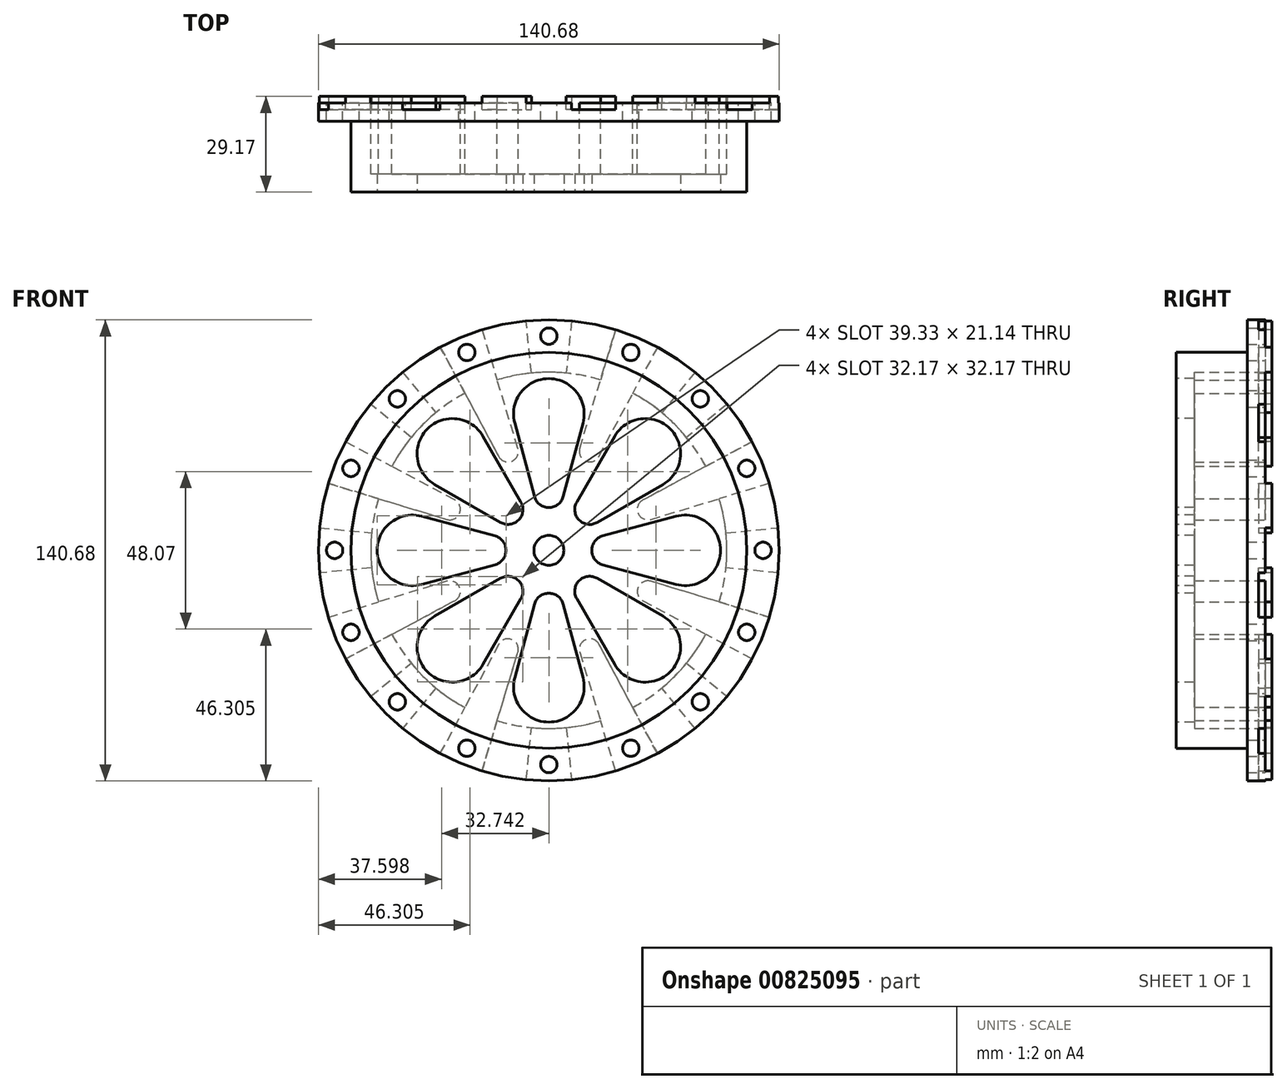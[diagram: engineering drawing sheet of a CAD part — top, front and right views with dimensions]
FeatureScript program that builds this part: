
annotation { "Feature Type Name" : "Feature", "Feature Type Description" : "" }
export const myFeature = defineFeature(function(context is Context, id is Id, definition is map)
    precondition{}
    {
        {
            var Q0;
            Q0=qCreatedBy(makeId("Right.planeOp"),FACE);
            var sketch = newSketch(context, id + "F0", { "sketchPlane" : qUnion([Q0])});
            skLineSegment(sketch, "E0", {"start": v(-27.17, 0) * mm, "end": v(-27.17, 60.4) * mm});
            skLineSegment(sketch, "E1", {"start": v(-21.65, 54.34) * mm, "end": v(-21.65, 0) * mm});
            skLineSegment(sketch, "E2", {"start": v(-21.65, 0) * mm, "end": v(-27.17, 0) * mm});
            skLineSegment(sketch, "E3", {"start": v(-27.17, 60.4) * mm, "end": v(-5.52, 60.4) * mm});
            skLineSegment(sketch, "E4", {"start": v(-21.65, 54.34) * mm, "end": v(0, 54.34) * mm});
            skLineSegment(sketch, "E5", {"start": v(-5.52, 60.4) * mm, "end": v(-5.52, 70.34) * mm});
            skLineSegment(sketch, "E6", {"start": v(-5.52, 70.34) * mm, "end": v(0, 70.34) * mm});
            skLineSegment(sketch, "E7", {"start": v(0, 70.34) * mm, "end": v(0, 54.34) * mm});
            skSolve(sketch);
        }
        {
            var Q0;
            Q0=makeQuery(id+"F0.imprint","IMPRINT",FACE,{"disambiguationData":[TD([[makeQuery(id+"F0.imprint","IMPRINT",EDGE,{"derivedFrom":sQuery(id+"F0.wireOp",EDGE,"E0")}),-1.0]])]});
            var Q1;
            Q1=sQuery(id+"F0.wireOp",EDGE,"E2");
            revolve(context, id + "F1", {"surfaceOperationType" : NewSurfaceOperationType.NEW, "entities" : qUnion([Q0]), "axis" : qUnion([Q1]), "revolveType" : RevolveType.FULL});
        }
        {
            var Q0;
            Q0=qCreatedBy(makeId("Front.planeOp"),FACE);
            var sketch = newSketch(context, id + "F2", { "sketchPlane" : qUnion([Q0])});
            skPoint(sketch, "E8", {"position": v(0, 65.37) * mm});
            skPoint(sketch, "E9.center", {"position": v(0, 0) * mm});
            skLineSegment(sketch, "E10.2.23.0", {"start": v(4.41, 16.46) * mm, "end": v(10.4, 38.84) * mm});
            skArc(sketch, "E11", {"start": v(-4.41, 16.46) * mm, "mid": v(0, 13.08) * mm, "end": v(4.41, 16.46) * mm});
            skArc(sketch, "E12", {"start": v(10.4, 38.84) * mm, "mid": v(0, 52.4) * mm, "end": v(-10.4, 38.84) * mm});
            skLineSegment(sketch, "E13", {"start": v(-10.4, 38.84) * mm, "end": v(-4.41, 16.46) * mm});
            skArc(sketch, "E14.1.0", {"start": v(-20.1, 34.83) * mm, "mid": v(-37.06, 37.06) * mm, "end": v(-34.83, 20.1) * mm});
            skLineSegment(sketch, "E14.1.1", {"start": v(-8.52, 14.76) * mm, "end": v(-20.1, 34.83) * mm});
            skArc(sketch, "E14.1.2", {"start": v(-14.76, 8.52) * mm, "mid": v(-9.25, 9.25) * mm, "end": v(-8.52, 14.76) * mm});
            skLineSegment(sketch, "E14.1.3", {"start": v(-34.83, 20.1) * mm, "end": v(-14.76, 8.52) * mm});
            skArc(sketch, "E14.2.0", {"start": v(-38.84, 10.4) * mm, "mid": v(-52.4, 0) * mm, "end": v(-38.84, -10.4) * mm});
            skLineSegment(sketch, "E14.2.1", {"start": v(-16.46, 4.41) * mm, "end": v(-38.84, 10.4) * mm});
            skArc(sketch, "E14.2.2", {"start": v(-16.46, -4.41) * mm, "mid": v(-13.08, 0) * mm, "end": v(-16.46, 4.41) * mm});
            skLineSegment(sketch, "E14.2.3", {"start": v(-38.84, -10.4) * mm, "end": v(-16.46, -4.41) * mm});
            skArc(sketch, "E14.3.0", {"start": v(-34.83, -20.1) * mm, "mid": v(-37.06, -37.06) * mm, "end": v(-20.1, -34.83) * mm});
            skLineSegment(sketch, "E14.3.1", {"start": v(-14.76, -8.52) * mm, "end": v(-34.83, -20.1) * mm});
            skArc(sketch, "E14.3.2", {"start": v(-8.52, -14.76) * mm, "mid": v(-9.25, -9.25) * mm, "end": v(-14.76, -8.52) * mm});
            skLineSegment(sketch, "E14.3.3", {"start": v(-20.1, -34.83) * mm, "end": v(-8.52, -14.76) * mm});
            skArc(sketch, "E14.4.0", {"start": v(-10.4, -38.84) * mm, "mid": v(0, -52.4) * mm, "end": v(10.4, -38.84) * mm});
            skLineSegment(sketch, "E14.4.1", {"start": v(-4.41, -16.46) * mm, "end": v(-10.4, -38.84) * mm});
            skArc(sketch, "E14.4.2", {"start": v(4.41, -16.46) * mm, "mid": v(0, -13.08) * mm, "end": v(-4.41, -16.46) * mm});
            skLineSegment(sketch, "E14.4.3", {"start": v(10.4, -38.84) * mm, "end": v(4.41, -16.46) * mm});
            skArc(sketch, "E14.5.0", {"start": v(20.1, -34.83) * mm, "mid": v(37.06, -37.06) * mm, "end": v(34.83, -20.1) * mm});
            skLineSegment(sketch, "E14.5.1", {"start": v(8.52, -14.76) * mm, "end": v(20.1, -34.83) * mm});
            skArc(sketch, "E14.5.2", {"start": v(14.76, -8.52) * mm, "mid": v(9.25, -9.25) * mm, "end": v(8.52, -14.76) * mm});
            skLineSegment(sketch, "E14.5.3", {"start": v(34.83, -20.1) * mm, "end": v(14.76, -8.52) * mm});
            skPoint(sketch, "E15.1.0", {"position": v(-25.02, 60.4) * mm});
            skPoint(sketch, "E15.2.0", {"position": v(-46.23, 46.23) * mm});
            skPoint(sketch, "E15.3.0", {"position": v(-60.4, 25.02) * mm});
            skPoint(sketch, "E15.4.0", {"position": v(-65.37, 0) * mm});
            skPoint(sketch, "E15.5.0", {"position": v(-60.4, -25.02) * mm});
            skPoint(sketch, "E16.0.6.0", {"position": v(-46.23, -46.23) * mm});
            skPoint(sketch, "E16.0.7.0", {"position": v(-25.02, -60.4) * mm});
            skPoint(sketch, "E16.0.8.0", {"position": v(0, -65.37) * mm});
            skPoint(sketch, "E16.0.9.0", {"position": v(25.02, -60.4) * mm});
            skPoint(sketch, "E16.0.10.0", {"position": v(46.23, -46.23) * mm});
            skPoint(sketch, "E16.0.11.0", {"position": v(60.4, -25.02) * mm});
            skCircle(sketch, "E17", {"center": v(0, 0) * mm, "radius": 4.57 * mm});
            skArc(sketch, "E18.3.6.0", {"start": v(38.84, -10.4) * mm, "mid": v(52.4, 0) * mm, "end": v(38.84, 10.4) * mm});
            skLineSegment(sketch, "E18.4.6.0", {"start": v(16.46, -4.41) * mm, "end": v(38.84, -10.4) * mm});
            skArc(sketch, "E18.7.6.0", {"start": v(16.46, 4.41) * mm, "mid": v(13.08, 0) * mm, "end": v(16.46, -4.41) * mm});
            skLineSegment(sketch, "E18.11.6.0", {"start": v(38.84, 10.4) * mm, "end": v(16.46, 4.41) * mm});
            skArc(sketch, "E18.3.7.0", {"start": v(34.83, 20.1) * mm, "mid": v(37.06, 37.06) * mm, "end": v(20.1, 34.83) * mm});
            skLineSegment(sketch, "E18.4.7.0", {"start": v(14.76, 8.52) * mm, "end": v(34.83, 20.1) * mm});
            skArc(sketch, "E18.7.7.0", {"start": v(8.52, 14.76) * mm, "mid": v(9.25, 9.25) * mm, "end": v(14.76, 8.52) * mm});
            skLineSegment(sketch, "E18.11.7.0", {"start": v(20.1, 34.83) * mm, "end": v(8.52, 14.76) * mm});
            skPoint(sketch, "E19.0.12.0", {"position": v(65.37, 0) * mm});
            skPoint(sketch, "E19.0.13.0", {"position": v(60.4, 25.02) * mm});
            skPoint(sketch, "E19.0.14.0", {"position": v(46.23, 46.23) * mm});
            skPoint(sketch, "E19.0.15.0", {"position": v(25.02, 60.4) * mm});
            skSolve(sketch);
        }
        {
            var Q0;
            Q0 = qSketchRegion(id + "F2", true);
            extrude(context, id + "F3", {"entities" : qUnion([Q0]), "operationType" : NewBodyOperationType.REMOVE, "oppositeDirection" : true, "depth" : 25 * mm, "offsetDistance" : 25 * mm, "hasSecondDirection" : true, "secondDirectionBound" : SecondDirectionBoundingType.THROUGH_ALL, "secondDirectionOppositeDirection" : false, "secondDirectionDepth" : 25 * mm});
        }
        {
            var Q0;
            Q0=sQuery(id+"F2.wireOp",VERTEX,"E8");
            var Q1;
            Q1=sQuery(id+"F2.wireOp",VERTEX,"E15.1.0");
            var Q2;
            Q2=sQuery(id+"F2.wireOp",VERTEX,"E15.2.0");
            var Q3;
            Q3=sQuery(id+"F2.wireOp",VERTEX,"E15.3.0");
            var Q4;
            Q4=sQuery(id+"F2.wireOp",VERTEX,"E15.4.0");
            var Q5;
            Q5=sQuery(id+"F2.wireOp",VERTEX,"E15.5.0");
            var Q6;
            Q6=sQuery(id+"F2.wireOp",VERTEX,"E16.0.6.0");
            var Q7;
            Q7=sQuery(id+"F2.wireOp",VERTEX,"E16.0.7.0");
            var Q8;
            Q8=sQuery(id+"F2.wireOp",VERTEX,"E16.0.8.0");
            var Q9;
            Q9=sQuery(id+"F2.wireOp",VERTEX,"E16.0.9.0");
            var Q10;
            Q10=sQuery(id+"F2.wireOp",VERTEX,"E16.0.10.0");
            var Q11;
            Q11=sQuery(id+"F2.wireOp",VERTEX,"E16.0.11.0");
            var Q12;
            Q12=sQuery(id+"F2.wireOp",VERTEX,"E19.0.12.0");
            var Q13;
            Q13=sQuery(id+"F2.wireOp",VERTEX,"E19.0.13.0");
            var Q14;
            Q14=sQuery(id+"F2.wireOp",VERTEX,"E19.0.14.0");
            var Q15;
            Q15=sQuery(id+"F2.wireOp",VERTEX,"E19.0.15.0");
            var Q16;
            Q16=makeQuery(id+"F1.opRevolve","SWEPT_BODY",BODY,{"disambiguationData":[OSD([sQuery(id+"F0.wireOp",EDGE,"E0"),sQuery(id+"F0.wireOp",EDGE,"E1"),sQuery(id+"F0.wireOp",EDGE,"E2"),sQuery(id+"F0.wireOp",EDGE,"E3"),sQuery(id+"F0.wireOp",EDGE,"E4"),sQuery(id+"F0.wireOp",EDGE,"E5"),sQuery(id+"F0.wireOp",EDGE,"E6"),sQuery(id+"F0.wireOp",EDGE,"E7")])]});
            hole(context, id + "F4", {"style" : HoleStyle.SIMPLE, "endStyle" : HoleEndStyle.THROUGH, "oppositeDirection" : true, "holeDiameter" : 5 * mm, "majorDiameter" : 5 * mm, "isTappedThrough" : true, "tappedDepth" : 12 * mm, "tapClearance" : 3, "locations" : qUnion([Q0, Q1, Q2, Q3, Q4, Q5, Q6, Q7, Q8, Q9, Q10, Q11, Q12, Q13, Q14, Q15]), "scope" : qUnion([Q16])});
        }
        {
            var Q0;
            Q0=qCreatedBy(makeId("Front.planeOp"),FACE);
            var sketch = newSketch(context, id + "F5", { "sketchPlane" : qUnion([Q0])});
            skLineSegment(sketch, "E20", {"start": v(9.44, 31.13) * mm, "end": v(15.77, 52) * mm});
            skPoint(sketch, "E21.orphan", {"position": v(20.42, 67.3) * mm});
            skPoint(sketch, "E22.MirrorP", {"position": v(33.16, 62.03) * mm});
            skLineSegment(sketch, "E23.MirrorCS", {"start": v(15.33, 28.69) * mm, "end": v(25.62, 47.92) * mm});
            skPoint(sketch, "E24.center.orphan", {"position": v(12.5, 30.2) * mm});
            skArc(sketch, "E25", {"start": v(9.44, 31.13) * mm, "mid": v(11.28, 27.24) * mm, "end": v(15.33, 28.69) * mm});
            skPoint(sketch, "E26", {"position": v(15.77, 52) * mm});
            skPoint(sketch, "E27", {"position": v(25.62, 47.92) * mm});
            skPoint(sketch, "E28.MirrorP", {"position": v(6.9, 70) * mm});
            skPoint(sketch, "E29.MirrorP", {"position": v(5.33, 54.08) * mm});
            skPoint(sketch, "E30.MirrorP", {"position": v(44.62, 54.37) * mm});
            skArc(sketch, "E31", {"start": v(15.77, 52) * mm, "mid": v(20.8, 50.2) * mm, "end": v(25.62, 47.92) * mm});
            skPoint(sketch, "E32.MirrorP", {"position": v(34.47, 42) * mm});
            skLineSegment(sketch, "E33", {"start": v(6.9, 70) * mm, "end": v(5.33, 54.08) * mm});
            skLineSegment(sketch, "E34", {"start": v(20.42, 67.3) * mm, "end": v(15.77, 52) * mm});
            skLineSegment(sketch, "E35", {"start": v(33.16, 62.03) * mm, "end": v(25.62, 47.92) * mm});
            skLineSegment(sketch, "E36", {"start": v(44.62, 54.37) * mm, "end": v(34.47, 42) * mm});
            skArc(sketch, "E37", {"start": v(5.33, 54.08) * mm, "mid": v(10.6, 53.3) * mm, "end": v(15.77, 52) * mm});
            skArc(sketch, "E38", {"start": v(25.62, 47.92) * mm, "mid": v(30.19, 45.18) * mm, "end": v(34.47, 42) * mm});
            skArc(sketch, "E39", {"start": v(33.16, 62.03) * mm, "mid": v(39.08, 58.48) * mm, "end": v(44.62, 54.37) * mm});
            skArc(sketch, "E40", {"start": v(6.9, 70) * mm, "mid": v(13.72, 68.99) * mm, "end": v(20.42, 67.3) * mm});
            skLineSegment(sketch, "E41.1.0", {"start": v(-6.9, 70) * mm, "end": v(-5.33, 54.08) * mm});
            skArc(sketch, "E41.1.1", {"start": v(-20.42, 67.3) * mm, "mid": v(-13.72, 68.99) * mm, "end": v(-6.9, 70) * mm});
            skLineSegment(sketch, "E41.1.2", {"start": v(-20.42, 67.3) * mm, "end": v(-15.77, 52) * mm});
            skArc(sketch, "E41.1.3", {"start": v(-15.77, 52) * mm, "mid": v(-10.6, 53.3) * mm, "end": v(-5.33, 54.08) * mm});
            skLineSegment(sketch, "E41.1.4", {"start": v(-9.44, 31.13) * mm, "end": v(-15.77, 52) * mm});
            skArc(sketch, "E41.1.5", {"start": v(-25.62, 47.92) * mm, "mid": v(-20.8, 50.2) * mm, "end": v(-15.77, 52) * mm});
            skLineSegment(sketch, "E41.1.6", {"start": v(-15.33, 28.69) * mm, "end": v(-25.62, 47.92) * mm});
            skArc(sketch, "E41.1.7", {"start": v(-15.33, 28.69) * mm, "mid": v(-11.28, 27.24) * mm, "end": v(-9.44, 31.13) * mm});
            skPoint(sketch, "E41.1.8", {"position": v(-12.5, 30.2) * mm});
            skLineSegment(sketch, "E41.1.9", {"start": v(-33.16, 62.03) * mm, "end": v(-25.62, 47.92) * mm});
            skArc(sketch, "E41.1.10", {"start": v(-44.62, 54.37) * mm, "mid": v(-39.08, 58.48) * mm, "end": v(-33.16, 62.03) * mm});
            skLineSegment(sketch, "E41.1.11", {"start": v(-44.62, 54.37) * mm, "end": v(-34.47, 42) * mm});
            skArc(sketch, "E41.1.12", {"start": v(-34.47, 42) * mm, "mid": v(-30.19, 45.18) * mm, "end": v(-25.62, 47.92) * mm});
            skLineSegment(sketch, "E41.2.0", {"start": v(-54.37, 44.62) * mm, "end": v(-42, 34.47) * mm});
            skArc(sketch, "E41.2.1", {"start": v(-62.03, 33.16) * mm, "mid": v(-58.48, 39.08) * mm, "end": v(-54.37, 44.62) * mm});
            skLineSegment(sketch, "E41.2.2", {"start": v(-62.03, 33.16) * mm, "end": v(-47.92, 25.62) * mm});
            skArc(sketch, "E41.2.3", {"start": v(-47.92, 25.62) * mm, "mid": v(-45.18, 30.19) * mm, "end": v(-42, 34.47) * mm});
            skLineSegment(sketch, "E41.2.4", {"start": v(-28.69, 15.33) * mm, "end": v(-47.92, 25.62) * mm});
            skArc(sketch, "E41.2.5", {"start": v(-52, 15.77) * mm, "mid": v(-50.2, 20.8) * mm, "end": v(-47.92, 25.62) * mm});
            skLineSegment(sketch, "E41.2.6", {"start": v(-31.13, 9.44) * mm, "end": v(-52, 15.77) * mm});
            skArc(sketch, "E41.2.7", {"start": v(-31.13, 9.44) * mm, "mid": v(-27.24, 11.28) * mm, "end": v(-28.69, 15.33) * mm});
            skPoint(sketch, "E41.2.8", {"position": v(-30.2, 12.5) * mm});
            skLineSegment(sketch, "E41.2.9", {"start": v(-67.3, 20.42) * mm, "end": v(-52, 15.77) * mm});
            skArc(sketch, "E41.2.10", {"start": v(-70, 6.9) * mm, "mid": v(-68.99, 13.72) * mm, "end": v(-67.3, 20.42) * mm});
            skLineSegment(sketch, "E41.2.11", {"start": v(-70, 6.9) * mm, "end": v(-54.08, 5.33) * mm});
            skArc(sketch, "E41.2.12", {"start": v(-54.08, 5.33) * mm, "mid": v(-53.3, 10.6) * mm, "end": v(-52, 15.77) * mm});
            skLineSegment(sketch, "E41.3.0", {"start": v(-70, -6.9) * mm, "end": v(-54.08, -5.33) * mm});
            skArc(sketch, "E41.3.1", {"start": v(-67.3, -20.42) * mm, "mid": v(-68.99, -13.72) * mm, "end": v(-70, -6.9) * mm});
            skLineSegment(sketch, "E41.3.2", {"start": v(-67.3, -20.42) * mm, "end": v(-52, -15.77) * mm});
            skArc(sketch, "E41.3.3", {"start": v(-52, -15.77) * mm, "mid": v(-53.3, -10.6) * mm, "end": v(-54.08, -5.33) * mm});
            skLineSegment(sketch, "E41.3.4", {"start": v(-31.13, -9.44) * mm, "end": v(-52, -15.77) * mm});
            skArc(sketch, "E41.3.5", {"start": v(-47.92, -25.62) * mm, "mid": v(-50.2, -20.8) * mm, "end": v(-52, -15.77) * mm});
            skLineSegment(sketch, "E41.3.6", {"start": v(-28.69, -15.33) * mm, "end": v(-47.92, -25.62) * mm});
            skArc(sketch, "E41.3.7", {"start": v(-28.69, -15.33) * mm, "mid": v(-27.24, -11.28) * mm, "end": v(-31.13, -9.44) * mm});
            skPoint(sketch, "E41.3.8", {"position": v(-30.2, -12.5) * mm});
            skLineSegment(sketch, "E41.3.9", {"start": v(-62.03, -33.16) * mm, "end": v(-47.92, -25.62) * mm});
            skArc(sketch, "E41.3.10", {"start": v(-54.37, -44.62) * mm, "mid": v(-58.48, -39.08) * mm, "end": v(-62.03, -33.16) * mm});
            skLineSegment(sketch, "E41.3.11", {"start": v(-54.37, -44.62) * mm, "end": v(-42, -34.47) * mm});
            skArc(sketch, "E41.3.12", {"start": v(-42, -34.47) * mm, "mid": v(-45.18, -30.19) * mm, "end": v(-47.92, -25.62) * mm});
            skLineSegment(sketch, "E41.4.0", {"start": v(-44.62, -54.37) * mm, "end": v(-34.47, -42) * mm});
            skArc(sketch, "E41.4.1", {"start": v(-33.16, -62.03) * mm, "mid": v(-39.08, -58.48) * mm, "end": v(-44.62, -54.37) * mm});
            skLineSegment(sketch, "E41.4.2", {"start": v(-33.16, -62.03) * mm, "end": v(-25.62, -47.92) * mm});
            skArc(sketch, "E41.4.3", {"start": v(-25.62, -47.92) * mm, "mid": v(-30.19, -45.18) * mm, "end": v(-34.47, -42) * mm});
            skLineSegment(sketch, "E41.4.4", {"start": v(-15.33, -28.69) * mm, "end": v(-25.62, -47.92) * mm});
            skArc(sketch, "E41.4.5", {"start": v(-15.77, -52) * mm, "mid": v(-20.8, -50.2) * mm, "end": v(-25.62, -47.92) * mm});
            skLineSegment(sketch, "E41.4.6", {"start": v(-9.44, -31.13) * mm, "end": v(-15.77, -52) * mm});
            skArc(sketch, "E41.4.7", {"start": v(-9.44, -31.13) * mm, "mid": v(-11.28, -27.24) * mm, "end": v(-15.33, -28.69) * mm});
            skPoint(sketch, "E41.4.8", {"position": v(-12.5, -30.2) * mm});
            skLineSegment(sketch, "E41.4.9", {"start": v(-20.42, -67.3) * mm, "end": v(-15.77, -52) * mm});
            skArc(sketch, "E41.4.10", {"start": v(-6.9, -70) * mm, "mid": v(-13.72, -68.99) * mm, "end": v(-20.42, -67.3) * mm});
            skLineSegment(sketch, "E41.4.11", {"start": v(-6.9, -70) * mm, "end": v(-5.33, -54.08) * mm});
            skArc(sketch, "E41.4.12", {"start": v(-5.33, -54.08) * mm, "mid": v(-10.6, -53.3) * mm, "end": v(-15.77, -52) * mm});
            skLineSegment(sketch, "E41.5.0", {"start": v(6.9, -70) * mm, "end": v(5.33, -54.08) * mm});
            skArc(sketch, "E41.5.1", {"start": v(20.42, -67.3) * mm, "mid": v(13.72, -68.99) * mm, "end": v(6.9, -70) * mm});
            skLineSegment(sketch, "E41.5.2", {"start": v(20.42, -67.3) * mm, "end": v(15.77, -52) * mm});
            skArc(sketch, "E41.5.3", {"start": v(15.77, -52) * mm, "mid": v(10.6, -53.3) * mm, "end": v(5.33, -54.08) * mm});
            skLineSegment(sketch, "E41.5.4", {"start": v(9.44, -31.13) * mm, "end": v(15.77, -52) * mm});
            skArc(sketch, "E41.5.5", {"start": v(25.62, -47.92) * mm, "mid": v(20.8, -50.2) * mm, "end": v(15.77, -52) * mm});
            skLineSegment(sketch, "E41.5.6", {"start": v(15.33, -28.69) * mm, "end": v(25.62, -47.92) * mm});
            skArc(sketch, "E41.5.7", {"start": v(15.33, -28.69) * mm, "mid": v(11.28, -27.24) * mm, "end": v(9.44, -31.13) * mm});
            skPoint(sketch, "E41.5.8", {"position": v(12.5, -30.2) * mm});
            skLineSegment(sketch, "E41.5.9", {"start": v(33.16, -62.03) * mm, "end": v(25.62, -47.92) * mm});
            skArc(sketch, "E41.5.10", {"start": v(44.62, -54.37) * mm, "mid": v(39.08, -58.48) * mm, "end": v(33.16, -62.03) * mm});
            skLineSegment(sketch, "E41.5.11", {"start": v(44.62, -54.37) * mm, "end": v(34.47, -42) * mm});
            skArc(sketch, "E41.5.12", {"start": v(34.47, -42) * mm, "mid": v(30.19, -45.18) * mm, "end": v(25.62, -47.92) * mm});
            skLineSegment(sketch, "E41.6.0", {"start": v(54.37, -44.62) * mm, "end": v(42, -34.47) * mm});
            skArc(sketch, "E41.6.1", {"start": v(62.03, -33.16) * mm, "mid": v(58.48, -39.08) * mm, "end": v(54.37, -44.62) * mm});
            skLineSegment(sketch, "E41.6.2", {"start": v(62.03, -33.16) * mm, "end": v(47.92, -25.62) * mm});
            skArc(sketch, "E41.6.3", {"start": v(47.92, -25.62) * mm, "mid": v(45.18, -30.19) * mm, "end": v(42, -34.47) * mm});
            skLineSegment(sketch, "E41.6.4", {"start": v(28.69, -15.33) * mm, "end": v(47.92, -25.62) * mm});
            skArc(sketch, "E41.6.5", {"start": v(52, -15.77) * mm, "mid": v(50.2, -20.8) * mm, "end": v(47.92, -25.62) * mm});
            skLineSegment(sketch, "E41.6.6", {"start": v(31.13, -9.44) * mm, "end": v(52, -15.77) * mm});
            skArc(sketch, "E41.6.7", {"start": v(31.13, -9.44) * mm, "mid": v(27.24, -11.28) * mm, "end": v(28.69, -15.33) * mm});
            skPoint(sketch, "E41.6.8", {"position": v(30.2, -12.5) * mm});
            skLineSegment(sketch, "E41.6.9", {"start": v(67.3, -20.42) * mm, "end": v(52, -15.77) * mm});
            skArc(sketch, "E41.6.10", {"start": v(70, -6.9) * mm, "mid": v(68.99, -13.72) * mm, "end": v(67.3, -20.42) * mm});
            skLineSegment(sketch, "E41.6.11", {"start": v(70, -6.9) * mm, "end": v(54.08, -5.33) * mm});
            skArc(sketch, "E41.6.12", {"start": v(54.08, -5.33) * mm, "mid": v(53.3, -10.6) * mm, "end": v(52, -15.77) * mm});
            skLineSegment(sketch, "E41.7.0", {"start": v(70, 6.9) * mm, "end": v(54.08, 5.33) * mm});
            skArc(sketch, "E41.7.1", {"start": v(67.3, 20.42) * mm, "mid": v(68.99, 13.72) * mm, "end": v(70, 6.9) * mm});
            skLineSegment(sketch, "E41.7.2", {"start": v(67.3, 20.42) * mm, "end": v(52, 15.77) * mm});
            skArc(sketch, "E41.7.3", {"start": v(52, 15.77) * mm, "mid": v(53.3, 10.6) * mm, "end": v(54.08, 5.33) * mm});
            skLineSegment(sketch, "E41.7.4", {"start": v(31.13, 9.44) * mm, "end": v(52, 15.77) * mm});
            skArc(sketch, "E41.7.5", {"start": v(47.92, 25.62) * mm, "mid": v(50.2, 20.8) * mm, "end": v(52, 15.77) * mm});
            skLineSegment(sketch, "E41.7.6", {"start": v(28.69, 15.33) * mm, "end": v(47.92, 25.62) * mm});
            skArc(sketch, "E41.7.7", {"start": v(28.69, 15.33) * mm, "mid": v(27.24, 11.28) * mm, "end": v(31.13, 9.44) * mm});
            skPoint(sketch, "E41.7.8", {"position": v(30.2, 12.5) * mm});
            skLineSegment(sketch, "E41.7.9", {"start": v(62.03, 33.16) * mm, "end": v(47.92, 25.62) * mm});
            skArc(sketch, "E41.7.10", {"start": v(54.37, 44.62) * mm, "mid": v(58.48, 39.08) * mm, "end": v(62.03, 33.16) * mm});
            skLineSegment(sketch, "E41.7.11", {"start": v(54.37, 44.62) * mm, "end": v(42, 34.47) * mm});
            skArc(sketch, "E41.7.12", {"start": v(42, 34.47) * mm, "mid": v(45.18, 30.19) * mm, "end": v(47.92, 25.62) * mm});
            skSolve(sketch);
        }
        {
            var Q0;
            Q0=makeQuery(id+"F5.imprint","IMPRINT",FACE,{"disambiguationData":[TD([[makeQuery(id+"F5.imprint","IMPRINT",EDGE,{"derivedFrom":sQuery(id+"F5.wireOp",EDGE,"E20")}),-1.0]])]});
            var sketch = newSketch(context, id + "F6", { "sketchPlane" : qUnion([Q0])});
            skLineSegment(sketch, "E42.0", {"start": v(15.33, 28.69) * mm, "end": v(25.62, 47.92) * mm});
            skArc(sketch, "E42.1", {"start": v(15.77, 52) * mm, "mid": v(20.8, 50.2) * mm, "end": v(25.62, 47.92) * mm});
            skLineSegment(sketch, "E42.2", {"start": v(9.44, 31.13) * mm, "end": v(15.77, 52) * mm});
            skArc(sketch, "E42.3", {"start": v(9.44, 31.13) * mm, "mid": v(11.28, 27.24) * mm, "end": v(15.33, 28.69) * mm});
            skArc(sketch, "E43.0.0", {"start": v(-15.77, 52) * mm, "mid": v(-20.8, 50.2) * mm, "end": v(-25.62, 47.92) * mm});
            skLineSegment(sketch, "E43.0.1", {"start": v(-25.62, 47.92) * mm, "end": v(-15.33, 28.69) * mm});
            skArc(sketch, "E43.0.2", {"start": v(-15.33, 28.69) * mm, "mid": v(-11.28, 27.24) * mm, "end": v(-9.44, 31.13) * mm});
            skLineSegment(sketch, "E43.0.3", {"start": v(-9.44, 31.13) * mm, "end": v(-15.77, 52) * mm});
            skArc(sketch, "E43.1.0", {"start": v(-47.92, 25.62) * mm, "mid": v(-50.2, 20.8) * mm, "end": v(-52, 15.77) * mm});
            skLineSegment(sketch, "E43.1.1", {"start": v(-52, 15.77) * mm, "end": v(-31.13, 9.44) * mm});
            skArc(sketch, "E43.1.2", {"start": v(-31.13, 9.44) * mm, "mid": v(-27.24, 11.28) * mm, "end": v(-28.69, 15.33) * mm});
            skLineSegment(sketch, "E43.1.3", {"start": v(-28.69, 15.33) * mm, "end": v(-47.92, 25.62) * mm});
            skArc(sketch, "E43.2.0", {"start": v(-52, -15.77) * mm, "mid": v(-50.2, -20.8) * mm, "end": v(-47.92, -25.62) * mm});
            skLineSegment(sketch, "E43.2.1", {"start": v(-47.92, -25.62) * mm, "end": v(-28.69, -15.33) * mm});
            skArc(sketch, "E43.2.2", {"start": v(-28.69, -15.33) * mm, "mid": v(-27.24, -11.28) * mm, "end": v(-31.13, -9.44) * mm});
            skLineSegment(sketch, "E43.2.3", {"start": v(-31.13, -9.44) * mm, "end": v(-52, -15.77) * mm});
            skArc(sketch, "E43.3.0", {"start": v(-25.62, -47.92) * mm, "mid": v(-20.8, -50.2) * mm, "end": v(-15.77, -52) * mm});
            skLineSegment(sketch, "E43.3.1", {"start": v(-15.77, -52) * mm, "end": v(-9.44, -31.13) * mm});
            skArc(sketch, "E43.3.2", {"start": v(-9.44, -31.13) * mm, "mid": v(-11.28, -27.24) * mm, "end": v(-15.33, -28.69) * mm});
            skLineSegment(sketch, "E43.3.3", {"start": v(-15.33, -28.69) * mm, "end": v(-25.62, -47.92) * mm});
            skArc(sketch, "E43.4.0", {"start": v(15.77, -52) * mm, "mid": v(20.8, -50.2) * mm, "end": v(25.62, -47.92) * mm});
            skLineSegment(sketch, "E43.4.1", {"start": v(25.62, -47.92) * mm, "end": v(15.33, -28.69) * mm});
            skArc(sketch, "E43.4.2", {"start": v(15.33, -28.69) * mm, "mid": v(11.28, -27.24) * mm, "end": v(9.44, -31.13) * mm});
            skLineSegment(sketch, "E43.4.3", {"start": v(9.44, -31.13) * mm, "end": v(15.77, -52) * mm});
            skArc(sketch, "E43.5.0", {"start": v(47.92, -25.62) * mm, "mid": v(50.2, -20.8) * mm, "end": v(52, -15.77) * mm});
            skLineSegment(sketch, "E43.5.1", {"start": v(52, -15.77) * mm, "end": v(31.13, -9.44) * mm});
            skArc(sketch, "E43.5.2", {"start": v(31.13, -9.44) * mm, "mid": v(27.24, -11.28) * mm, "end": v(28.69, -15.33) * mm});
            skLineSegment(sketch, "E43.5.3", {"start": v(28.69, -15.33) * mm, "end": v(47.92, -25.62) * mm});
            skArc(sketch, "E43.6.0", {"start": v(52, 15.77) * mm, "mid": v(50.2, 20.8) * mm, "end": v(47.92, 25.62) * mm});
            skLineSegment(sketch, "E43.6.1", {"start": v(47.92, 25.62) * mm, "end": v(28.69, 15.33) * mm});
            skArc(sketch, "E43.6.2", {"start": v(28.69, 15.33) * mm, "mid": v(27.24, 11.28) * mm, "end": v(31.13, 9.44) * mm});
            skLineSegment(sketch, "E43.6.3", {"start": v(31.13, 9.44) * mm, "end": v(52, 15.77) * mm});
            skSolve(sketch);
        }
        {
            var Q0;
            Q0=makeQuery(id+"F5.imprint","IMPRINT",FACE,{"disambiguationData":[TD([[makeQuery(id+"F5.imprint","IMPRINT",EDGE,{"derivedFrom":sQuery(id+"F5.wireOp",EDGE,"E33")}),1.0]])]});
            var sketch = newSketch(context, id + "F7", { "sketchPlane" : qUnion([Q0])});
            skLineSegment(sketch, "E44.0.0", {"start": v(15.77, 52) * mm, "end": v(20.42, 67.3) * mm});
            skArc(sketch, "E44.0.1", {"start": v(20.42, 67.3) * mm, "mid": v(13.72, 68.99) * mm, "end": v(6.9, 70) * mm});
            skLineSegment(sketch, "E44.0.2", {"start": v(6.9, 70) * mm, "end": v(5.33, 54.08) * mm});
            skArc(sketch, "E44.0.3", {"start": v(5.33, 54.08) * mm, "mid": v(10.6, 53.3) * mm, "end": v(15.77, 52) * mm});
            skLineSegment(sketch, "E44.1.0", {"start": v(-44.62, 54.37) * mm, "end": v(-34.47, 42) * mm});
            skArc(sketch, "E44.1.1", {"start": v(-34.47, 42) * mm, "mid": v(-30.19, 45.18) * mm, "end": v(-25.62, 47.92) * mm});
            skLineSegment(sketch, "E44.1.2", {"start": v(-25.62, 47.92) * mm, "end": v(-33.16, 62.03) * mm});
            skArc(sketch, "E44.1.3", {"start": v(-33.16, 62.03) * mm, "mid": v(-39.08, 58.48) * mm, "end": v(-44.62, 54.37) * mm});
            skLineSegment(sketch, "E44.2.0", {"start": v(-70, 6.9) * mm, "end": v(-54.08, 5.33) * mm});
            skArc(sketch, "E44.2.1", {"start": v(-54.08, 5.33) * mm, "mid": v(-53.3, 10.6) * mm, "end": v(-52, 15.77) * mm});
            skLineSegment(sketch, "E44.2.2", {"start": v(-52, 15.77) * mm, "end": v(-67.3, 20.42) * mm});
            skArc(sketch, "E44.2.3", {"start": v(-67.3, 20.42) * mm, "mid": v(-68.99, 13.72) * mm, "end": v(-70, 6.9) * mm});
            skLineSegment(sketch, "E44.3.0", {"start": v(-54.37, -44.62) * mm, "end": v(-42, -34.47) * mm});
            skArc(sketch, "E44.3.1", {"start": v(-42, -34.47) * mm, "mid": v(-45.18, -30.19) * mm, "end": v(-47.92, -25.62) * mm});
            skLineSegment(sketch, "E44.3.2", {"start": v(-47.92, -25.62) * mm, "end": v(-62.03, -33.16) * mm});
            skArc(sketch, "E44.3.3", {"start": v(-62.03, -33.16) * mm, "mid": v(-58.48, -39.08) * mm, "end": v(-54.37, -44.62) * mm});
            skLineSegment(sketch, "E44.4.0", {"start": v(-6.9, -70) * mm, "end": v(-5.33, -54.08) * mm});
            skArc(sketch, "E44.4.1", {"start": v(-5.33, -54.08) * mm, "mid": v(-10.6, -53.3) * mm, "end": v(-15.77, -52) * mm});
            skLineSegment(sketch, "E44.4.2", {"start": v(-15.77, -52) * mm, "end": v(-20.42, -67.3) * mm});
            skArc(sketch, "E44.4.3", {"start": v(-20.42, -67.3) * mm, "mid": v(-13.72, -68.99) * mm, "end": v(-6.9, -70) * mm});
            skLineSegment(sketch, "E44.5.0", {"start": v(44.62, -54.37) * mm, "end": v(34.47, -42) * mm});
            skArc(sketch, "E44.5.1", {"start": v(34.47, -42) * mm, "mid": v(30.19, -45.18) * mm, "end": v(25.62, -47.92) * mm});
            skLineSegment(sketch, "E44.5.2", {"start": v(25.62, -47.92) * mm, "end": v(33.16, -62.03) * mm});
            skArc(sketch, "E44.5.3", {"start": v(33.16, -62.03) * mm, "mid": v(39.08, -58.48) * mm, "end": v(44.62, -54.37) * mm});
            skLineSegment(sketch, "E44.6.0", {"start": v(70, -6.9) * mm, "end": v(54.08, -5.33) * mm});
            skArc(sketch, "E44.6.1", {"start": v(54.08, -5.33) * mm, "mid": v(53.3, -10.6) * mm, "end": v(52, -15.77) * mm});
            skLineSegment(sketch, "E44.6.2", {"start": v(52, -15.77) * mm, "end": v(67.3, -20.42) * mm});
            skArc(sketch, "E44.6.3", {"start": v(67.3, -20.42) * mm, "mid": v(68.99, -13.72) * mm, "end": v(70, -6.9) * mm});
            skLineSegment(sketch, "E44.7.0", {"start": v(54.37, 44.62) * mm, "end": v(42, 34.47) * mm});
            skArc(sketch, "E44.7.1", {"start": v(42, 34.47) * mm, "mid": v(45.18, 30.19) * mm, "end": v(47.92, 25.62) * mm});
            skLineSegment(sketch, "E44.7.2", {"start": v(47.92, 25.62) * mm, "end": v(62.03, 33.16) * mm});
            skArc(sketch, "E44.7.3", {"start": v(62.03, 33.16) * mm, "mid": v(58.48, 39.08) * mm, "end": v(54.37, 44.62) * mm});
            skSolve(sketch);
        }
        {
            var Q0;
            Q0=makeQuery(id+"F5.imprint","IMPRINT",FACE,{"disambiguationData":[TD([[makeQuery(id+"F5.imprint","IMPRINT",EDGE,{"derivedFrom":sQuery(id+"F5.wireOp",EDGE,"E35")}),1.0]])]});
            var sketch = newSketch(context, id + "F8", { "sketchPlane" : qUnion([Q0])});
            skLineSegment(sketch, "E45.0.0", {"start": v(33.16, 62.03) * mm, "end": v(25.62, 47.92) * mm});
            skArc(sketch, "E45.0.1", {"start": v(25.62, 47.92) * mm, "mid": v(30.19, 45.18) * mm, "end": v(34.47, 42) * mm});
            skLineSegment(sketch, "E45.0.2", {"start": v(34.47, 42) * mm, "end": v(44.62, 54.37) * mm});
            skArc(sketch, "E45.0.3", {"start": v(44.62, 54.37) * mm, "mid": v(39.08, 58.48) * mm, "end": v(33.16, 62.03) * mm});
            skLineSegment(sketch, "E45.1.0", {"start": v(-20.42, 67.3) * mm, "end": v(-15.77, 52) * mm});
            skArc(sketch, "E45.1.1", {"start": v(-15.77, 52) * mm, "mid": v(-10.6, 53.3) * mm, "end": v(-5.33, 54.08) * mm});
            skLineSegment(sketch, "E45.1.2", {"start": v(-5.33, 54.08) * mm, "end": v(-6.9, 70) * mm});
            skArc(sketch, "E45.1.3", {"start": v(-6.9, 70) * mm, "mid": v(-13.72, 68.99) * mm, "end": v(-20.42, 67.3) * mm});
            skLineSegment(sketch, "E45.2.0", {"start": v(-62.03, 33.16) * mm, "end": v(-47.92, 25.62) * mm});
            skArc(sketch, "E45.2.1", {"start": v(-47.92, 25.62) * mm, "mid": v(-45.18, 30.19) * mm, "end": v(-42, 34.47) * mm});
            skLineSegment(sketch, "E45.2.2", {"start": v(-42, 34.47) * mm, "end": v(-54.37, 44.62) * mm});
            skArc(sketch, "E45.2.3", {"start": v(-54.37, 44.62) * mm, "mid": v(-58.48, 39.08) * mm, "end": v(-62.03, 33.16) * mm});
            skLineSegment(sketch, "E45.3.0", {"start": v(-67.3, -20.42) * mm, "end": v(-52, -15.77) * mm});
            skArc(sketch, "E45.3.1", {"start": v(-52, -15.77) * mm, "mid": v(-53.3, -10.6) * mm, "end": v(-54.08, -5.33) * mm});
            skLineSegment(sketch, "E45.3.2", {"start": v(-54.08, -5.33) * mm, "end": v(-70, -6.9) * mm});
            skArc(sketch, "E45.3.3", {"start": v(-70, -6.9) * mm, "mid": v(-68.99, -13.72) * mm, "end": v(-67.3, -20.42) * mm});
            skLineSegment(sketch, "E45.4.0", {"start": v(-33.16, -62.03) * mm, "end": v(-25.62, -47.92) * mm});
            skArc(sketch, "E45.4.1", {"start": v(-25.62, -47.92) * mm, "mid": v(-30.19, -45.18) * mm, "end": v(-34.47, -42) * mm});
            skLineSegment(sketch, "E45.4.2", {"start": v(-34.47, -42) * mm, "end": v(-44.62, -54.37) * mm});
            skArc(sketch, "E45.4.3", {"start": v(-44.62, -54.37) * mm, "mid": v(-39.08, -58.48) * mm, "end": v(-33.16, -62.03) * mm});
            skLineSegment(sketch, "E45.5.0", {"start": v(20.42, -67.3) * mm, "end": v(15.77, -52) * mm});
            skArc(sketch, "E45.5.1", {"start": v(15.77, -52) * mm, "mid": v(10.6, -53.3) * mm, "end": v(5.33, -54.08) * mm});
            skLineSegment(sketch, "E45.5.2", {"start": v(5.33, -54.08) * mm, "end": v(6.9, -70) * mm});
            skArc(sketch, "E45.5.3", {"start": v(6.9, -70) * mm, "mid": v(13.72, -68.99) * mm, "end": v(20.42, -67.3) * mm});
            skLineSegment(sketch, "E45.6.0", {"start": v(62.03, -33.16) * mm, "end": v(47.92, -25.62) * mm});
            skArc(sketch, "E45.6.1", {"start": v(47.92, -25.62) * mm, "mid": v(45.18, -30.19) * mm, "end": v(42, -34.47) * mm});
            skLineSegment(sketch, "E45.6.2", {"start": v(42, -34.47) * mm, "end": v(54.37, -44.62) * mm});
            skArc(sketch, "E45.6.3", {"start": v(54.37, -44.62) * mm, "mid": v(58.48, -39.08) * mm, "end": v(62.03, -33.16) * mm});
            skLineSegment(sketch, "E45.7.0", {"start": v(67.3, 20.42) * mm, "end": v(52, 15.77) * mm});
            skArc(sketch, "E45.7.1", {"start": v(52, 15.77) * mm, "mid": v(53.3, 10.6) * mm, "end": v(54.08, 5.33) * mm});
            skLineSegment(sketch, "E45.7.2", {"start": v(54.08, 5.33) * mm, "end": v(70, 6.9) * mm});
            skArc(sketch, "E45.7.3", {"start": v(70, 6.9) * mm, "mid": v(68.99, 13.72) * mm, "end": v(67.3, 20.42) * mm});
            skSolve(sketch);
        }
        {
            var Q0;
            Q0 = qSketchRegion(id + "F6", true);
            var Q1;
            Q1=makeQuery(id+"F1.opRevolve","SWEPT_FACE",FACE,{"disambiguationData":[OSD([sQuery(id+"F0.wireOp",EDGE,"E1")])]});
            extrude(context, id + "F9", {"entities" : qUnion([Q0]), "operationType" : NewBodyOperationType.ADD, "endBound" : BoundingType.UP_TO_SURFACE, "depth" : 25 * mm, "endBoundEntityFace" : qUnion([Q1]), "offsetDistance" : 25 * mm});
        }
        {
            var Q0;
            Q0 = qSketchRegion(id + "F7", true);
            extrude(context, id + "F10", {"entities" : qUnion([Q0]), "operationType" : NewBodyOperationType.REMOVE, "oppositeDirection" : true, "depth" : -2 * mm, "offsetDistance" : 25 * mm});
        }
        {
            var Q0;
            Q0 = qSketchRegion(id + "F8", true);
            extrude(context, id + "F11", {"entities" : qUnion([Q0]), "operationType" : NewBodyOperationType.ADD, "depth" : -2 * mm, "offsetDistance" : 25 * mm});
        }
    });
